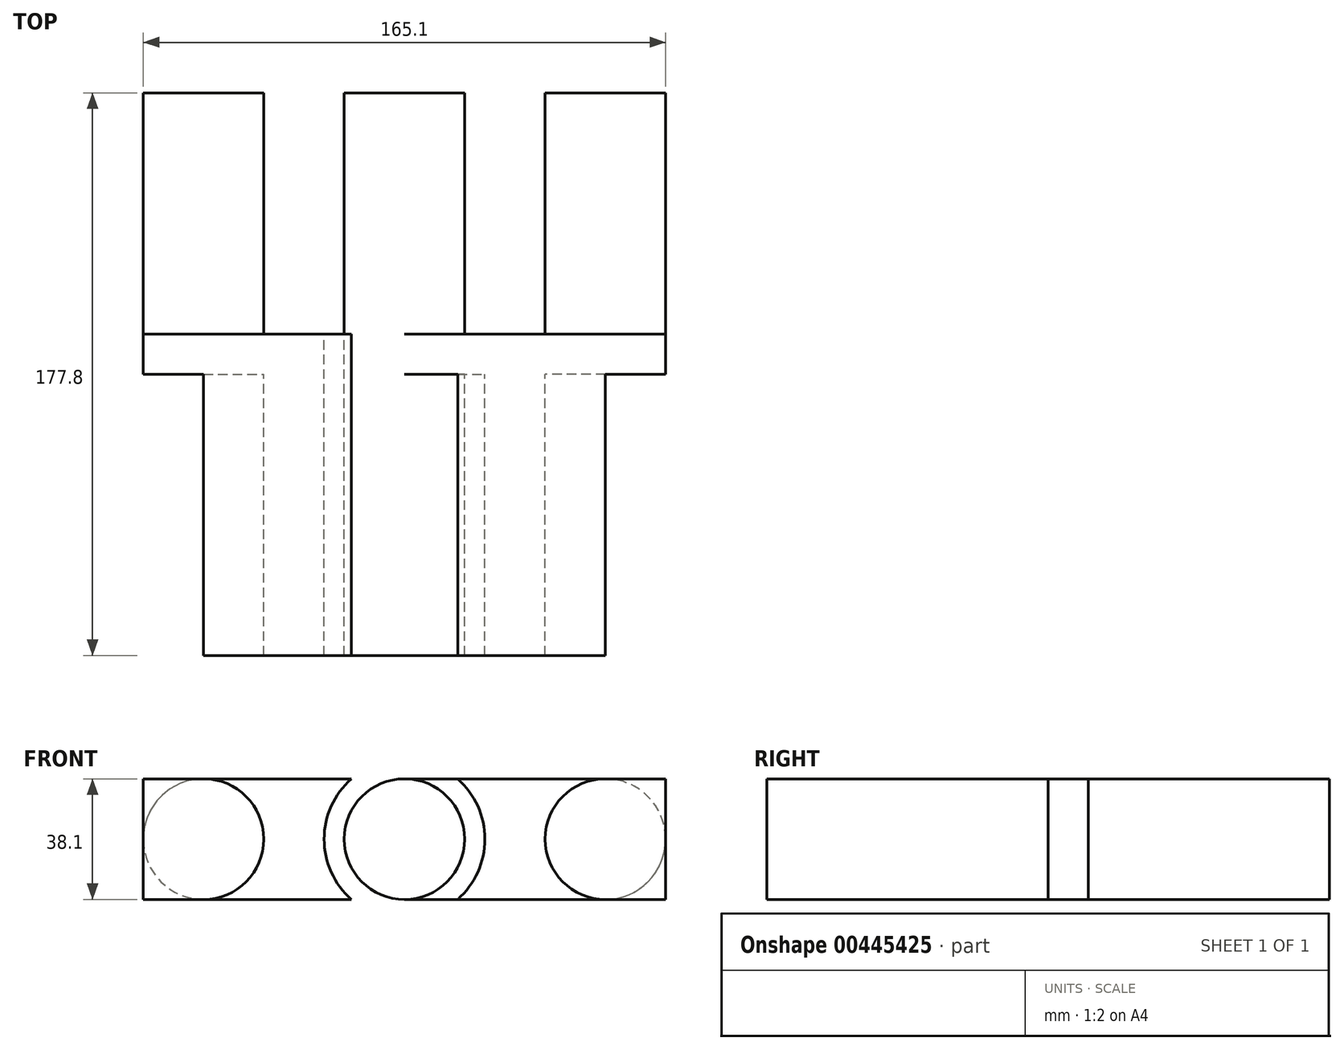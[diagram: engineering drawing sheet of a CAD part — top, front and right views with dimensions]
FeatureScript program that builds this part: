
annotation { "Feature Type Name" : "Feature", "Feature Type Description" : "" }
export const myFeature = defineFeature(function(context is Context, id is Id, definition is map)
    precondition{}
    {
        {
            var Q0;
            Q0=qCreatedBy(makeId("Front.planeOp"),FACE);
            var sketch = newSketch(context, id + "F0", { "sketchPlane" : qUnion([Q0])});
            skLineSegment(sketch, "E0.bottom", {"start": v(82.55, 19.05) * mm, "end": v(-82.55, 19.05) * mm});
            skLineSegment(sketch, "E0.top", {"start": v(82.55, -19.05) * mm, "end": v(-82.55, -19.05) * mm});
            skLineSegment(sketch, "E0.left", {"start": v(82.55, 19.05) * mm, "end": v(82.55, -19.05) * mm});
            skLineSegment(sketch, "E0.right", {"start": v(-82.55, 19.05) * mm, "end": v(-82.55, -19.05) * mm});
            skPoint(sketch, "E0.middle", {"position": v(0, 0) * mm});
            skCircle(sketch, "E1", {"center": v(0, 0) * mm, "radius": 25.4 * mm});
            skCircle(sketch, "E2", {"center": v(0, 0) * mm, "radius": 19.05 * mm});
            skPoint(sketch, "E3", {"position": v(63.5, 0) * mm});
            skPoint(sketch, "E4", {"position": v(-63.5, 0) * mm});
            skCircle(sketch, "E5", {"center": v(63.5, 0) * mm, "radius": 19.05 * mm});
            skCircle(sketch, "E6", {"center": v(-63.5, 0) * mm, "radius": 19.05 * mm});
            skSolve(sketch);
        }
        {
            var Q0;
            {var subQ0=sQuery(id+"F0.wireOp",EDGE,"E1");var subQ1=sQuery(id+"F0.wireOp",EDGE,"E0.bottom");var subQ2=makeQuery(id+"F0.imprint","INTERSECT",VERTEX,{"disambiguationData":[OD(0.0)],"derivedFrom":[subQ1,subQ0]});Q0=makeQuery(id+"F0.imprint","IMPRINT",FACE,{"disambiguationData":[TD([[makeQuery(id+"F0.imprint","IMPRINT",EDGE,{"disambiguationData":[TD([[subQ2,-1.0]])],"derivedFrom":subQ1}),1.0]])]});}
            var Q1;
            {var subQ0=sQuery(id+"F0.wireOp",EDGE,"E1");var subQ1=sQuery(id+"F0.wireOp",EDGE,"E0.bottom");var subQ2=makeQuery(id+"F0.imprint","INTERSECT",VERTEX,{"disambiguationData":[OD(0.0)],"derivedFrom":[subQ1,subQ0]});Q1=makeQuery(id+"F0.imprint","IMPRINT",FACE,{"disambiguationData":[TD([[makeQuery(id+"F0.imprint","IMPRINT",EDGE,{"disambiguationData":[TD([[subQ2,-1.0]])],"derivedFrom":subQ1}),-1.0]])]});}
            var Q2;
            {var subQ0=sQuery(id+"F0.wireOp",EDGE,"E1");var subQ1=sQuery(id+"F0.wireOp",EDGE,"E0.bottom");var subQ2=makeQuery(id+"F0.imprint","INTERSECT",VERTEX,{"disambiguationData":[OD(1.0)],"derivedFrom":[subQ1,subQ0]});Q2=makeQuery(id+"F0.imprint","IMPRINT",FACE,{"disambiguationData":[TD([[makeQuery(id+"F0.imprint","IMPRINT",EDGE,{"disambiguationData":[TD([[subQ2,1.0]])],"derivedFrom":subQ1}),1.0]])]});}
            var Q3;
            {var subQ0=sQuery(id+"F0.wireOp",EDGE,"E1");var subQ1=sQuery(id+"F0.wireOp",EDGE,"E0.top");var subQ2=makeQuery(id+"F0.imprint","INTERSECT",VERTEX,{"disambiguationData":[OD(0.0)],"derivedFrom":[subQ1,subQ0]});Q3=makeQuery(id+"F0.imprint","IMPRINT",FACE,{"disambiguationData":[TD([[makeQuery(id+"F0.imprint","IMPRINT",EDGE,{"disambiguationData":[TD([[subQ2,-1.0]])],"derivedFrom":subQ1}),1.0]])]});}
            var Q4;
            {var subQ0=sQuery(id+"F0.wireOp",EDGE,"E2");var subQ1=makeQuery(id+"F0.imprint","INTERSECT",VERTEX,{"derivedFrom":[sQuery(id+"F0.wireOp",EDGE,"E0.bottom"),subQ0]});Q4=makeQuery(id+"F0.imprint","IMPRINT",FACE,{"disambiguationData":[TD([[makeQuery(id+"F0.imprint","IMPRINT",EDGE,{"disambiguationData":[TD([[subQ1,-1.0]])],"derivedFrom":subQ0}),1.0]])]});}
            extrude(context, id + "F1", {"entities" : qUnion([Q0, Q1, Q2, Q3, Q4]), "depth" : 101.6 * mm});
        }
        {
            var Q0;
            {var subQ0=sQuery(id+"F0.wireOp",EDGE,"E5");var subQ1=sQuery(id+"F0.wireOp",EDGE,"E0.bottom");var subQ2=makeQuery(id+"F0.imprint","INTERSECT",VERTEX,{"derivedFrom":[subQ1,subQ0]});Q0=makeQuery(id+"F0.imprint","IMPRINT",FACE,{"disambiguationData":[TD([[makeQuery(id+"F0.imprint","IMPRINT",EDGE,{"disambiguationData":[TD([[subQ2,-1.0]])],"derivedFrom":subQ1}),1.0]])]});}
            var Q1;
            {var subQ0=sQuery(id+"F0.wireOp",EDGE,"E0.left");var subQ1=sQuery(id+"F0.wireOp",EDGE,"E0.top");var subQ2=makeQuery(id+"F0.imprint","INTERSECT",VERTEX,{"derivedFrom":[subQ1,subQ0]});Q1=makeQuery(id+"F0.imprint","IMPRINT",FACE,{"disambiguationData":[TD([[makeQuery(id+"F0.imprint","IMPRINT",EDGE,{"disambiguationData":[TD([[subQ2,-1.0]])],"derivedFrom":subQ1}),-1.0]])]});}
            var Q2;
            {var subQ0=sQuery(id+"F0.wireOp",EDGE,"E5");var subQ1=makeQuery(id+"F0.imprint","INTERSECT",VERTEX,{"derivedFrom":[sQuery(id+"F0.wireOp",EDGE,"E0.bottom"),subQ0]});Q2=makeQuery(id+"F0.imprint","IMPRINT",FACE,{"disambiguationData":[TD([[makeQuery(id+"F0.imprint","IMPRINT",EDGE,{"disambiguationData":[TD([[subQ1,1.0]])],"derivedFrom":subQ0}),1.0]])]});}
            var Q3;
            {var subQ0=sQuery(id+"F0.wireOp",EDGE,"E0.left");var subQ1=sQuery(id+"F0.wireOp",EDGE,"E0.bottom");var subQ2=makeQuery(id+"F0.imprint","INTERSECT",VERTEX,{"derivedFrom":[subQ1,subQ0]});Q3=makeQuery(id+"F0.imprint","IMPRINT",FACE,{"disambiguationData":[TD([[makeQuery(id+"F0.imprint","IMPRINT",EDGE,{"disambiguationData":[TD([[subQ2,-1.0]])],"derivedFrom":subQ1}),1.0]])]});}
            var Q4;
            {var subQ0=sQuery(id+"F0.wireOp",EDGE,"E1");var subQ1=sQuery(id+"F0.wireOp",EDGE,"E0.bottom");var subQ2=makeQuery(id+"F0.imprint","INTERSECT",VERTEX,{"disambiguationData":[OD(0.0)],"derivedFrom":[subQ1,subQ0]});Q4=makeQuery(id+"F0.imprint","IMPRINT",FACE,{"disambiguationData":[TD([[makeQuery(id+"F0.imprint","IMPRINT",EDGE,{"disambiguationData":[TD([[subQ2,-1.0]])],"derivedFrom":subQ1}),1.0]])]});}
            var Q5;
            {var subQ0=sQuery(id+"F0.wireOp",EDGE,"E2");var subQ1=makeQuery(id+"F0.imprint","INTERSECT",VERTEX,{"derivedFrom":[sQuery(id+"F0.wireOp",EDGE,"E0.bottom"),subQ0]});Q5=makeQuery(id+"F0.imprint","IMPRINT",FACE,{"disambiguationData":[TD([[makeQuery(id+"F0.imprint","IMPRINT",EDGE,{"disambiguationData":[TD([[subQ1,-1.0]])],"derivedFrom":subQ0}),1.0]])]});}
            var Q6;
            {var subQ0=sQuery(id+"F0.wireOp",EDGE,"E1");var subQ1=sQuery(id+"F0.wireOp",EDGE,"E0.bottom");var subQ2=makeQuery(id+"F0.imprint","INTERSECT",VERTEX,{"disambiguationData":[OD(1.0)],"derivedFrom":[subQ1,subQ0]});Q6=makeQuery(id+"F0.imprint","IMPRINT",FACE,{"disambiguationData":[TD([[makeQuery(id+"F0.imprint","IMPRINT",EDGE,{"disambiguationData":[TD([[subQ2,1.0]])],"derivedFrom":subQ1}),1.0]])]});}
            var Q7;
            {var subQ0=sQuery(id+"F0.wireOp",EDGE,"E1");var subQ1=sQuery(id+"F0.wireOp",EDGE,"E0.bottom");var subQ2=makeQuery(id+"F0.imprint","INTERSECT",VERTEX,{"disambiguationData":[OD(1.0)],"derivedFrom":[subQ1,subQ0]});Q7=makeQuery(id+"F0.imprint","IMPRINT",FACE,{"disambiguationData":[TD([[makeQuery(id+"F0.imprint","IMPRINT",EDGE,{"disambiguationData":[TD([[subQ2,-1.0]])],"derivedFrom":subQ1}),1.0]])]});}
            var Q8;
            {var subQ0=sQuery(id+"F0.wireOp",EDGE,"E6");var subQ1=makeQuery(id+"F0.imprint","INTERSECT",VERTEX,{"derivedFrom":[sQuery(id+"F0.wireOp",EDGE,"E0.bottom"),subQ0]});Q8=makeQuery(id+"F0.imprint","IMPRINT",FACE,{"disambiguationData":[TD([[makeQuery(id+"F0.imprint","IMPRINT",EDGE,{"disambiguationData":[TD([[subQ1,-1.0]])],"derivedFrom":subQ0}),1.0]])]});}
            var Q9;
            {var subQ0=sQuery(id+"F0.wireOp",EDGE,"E0.right");var subQ1=sQuery(id+"F0.wireOp",EDGE,"E0.bottom");var subQ2=makeQuery(id+"F0.imprint","INTERSECT",VERTEX,{"derivedFrom":[subQ1,subQ0]});Q9=makeQuery(id+"F0.imprint","IMPRINT",FACE,{"disambiguationData":[TD([[makeQuery(id+"F0.imprint","IMPRINT",EDGE,{"disambiguationData":[TD([[subQ2,1.0]])],"derivedFrom":subQ1}),1.0]])]});}
            var Q10;
            {var subQ0=sQuery(id+"F0.wireOp",EDGE,"E0.right");var subQ1=sQuery(id+"F0.wireOp",EDGE,"E0.top");var subQ2=makeQuery(id+"F0.imprint","INTERSECT",VERTEX,{"derivedFrom":[subQ1,subQ0]});Q10=makeQuery(id+"F0.imprint","IMPRINT",FACE,{"disambiguationData":[TD([[makeQuery(id+"F0.imprint","IMPRINT",EDGE,{"disambiguationData":[TD([[subQ2,1.0]])],"derivedFrom":subQ1}),-1.0]])]});}
            extrude(context, id + "F2", {"entities" : qUnion([Q0, Q1, Q2, Q3, Q4, Q5, Q6, Q7, Q8, Q9, Q10]), "operationType" : NewBodyOperationType.ADD, "depth" : 12.7 * mm});
        }
        {
            var Q0;
            {var subQ0=sQuery(id+"F0.wireOp",EDGE,"E2");var subQ1=makeQuery(id+"F0.imprint","INTERSECT",VERTEX,{"derivedFrom":[sQuery(id+"F0.wireOp",EDGE,"E0.bottom"),subQ0]});Q0=makeQuery(id+"F0.imprint","IMPRINT",FACE,{"disambiguationData":[TD([[makeQuery(id+"F0.imprint","IMPRINT",EDGE,{"disambiguationData":[TD([[subQ1,-1.0]])],"derivedFrom":subQ0}),1.0]])]});}
            var Q1;
            {var subQ0=sQuery(id+"F0.wireOp",EDGE,"E6");var subQ1=makeQuery(id+"F0.imprint","INTERSECT",VERTEX,{"derivedFrom":[sQuery(id+"F0.wireOp",EDGE,"E0.bottom"),subQ0]});Q1=makeQuery(id+"F0.imprint","IMPRINT",FACE,{"disambiguationData":[TD([[makeQuery(id+"F0.imprint","IMPRINT",EDGE,{"disambiguationData":[TD([[subQ1,-1.0]])],"derivedFrom":subQ0}),1.0]])]});}
            var Q2;
            {var subQ0=sQuery(id+"F0.wireOp",EDGE,"E5");var subQ1=makeQuery(id+"F0.imprint","INTERSECT",VERTEX,{"derivedFrom":[sQuery(id+"F0.wireOp",EDGE,"E0.bottom"),subQ0]});Q2=makeQuery(id+"F0.imprint","IMPRINT",FACE,{"disambiguationData":[TD([[makeQuery(id+"F0.imprint","IMPRINT",EDGE,{"disambiguationData":[TD([[subQ1,1.0]])],"derivedFrom":subQ0}),1.0]])]});}
            extrude(context, id + "F3", {"entities" : qUnion([Q0, Q1, Q2]), "operationType" : NewBodyOperationType.ADD, "oppositeDirection" : true, "depth" : 76.2 * mm});
        }
    });
